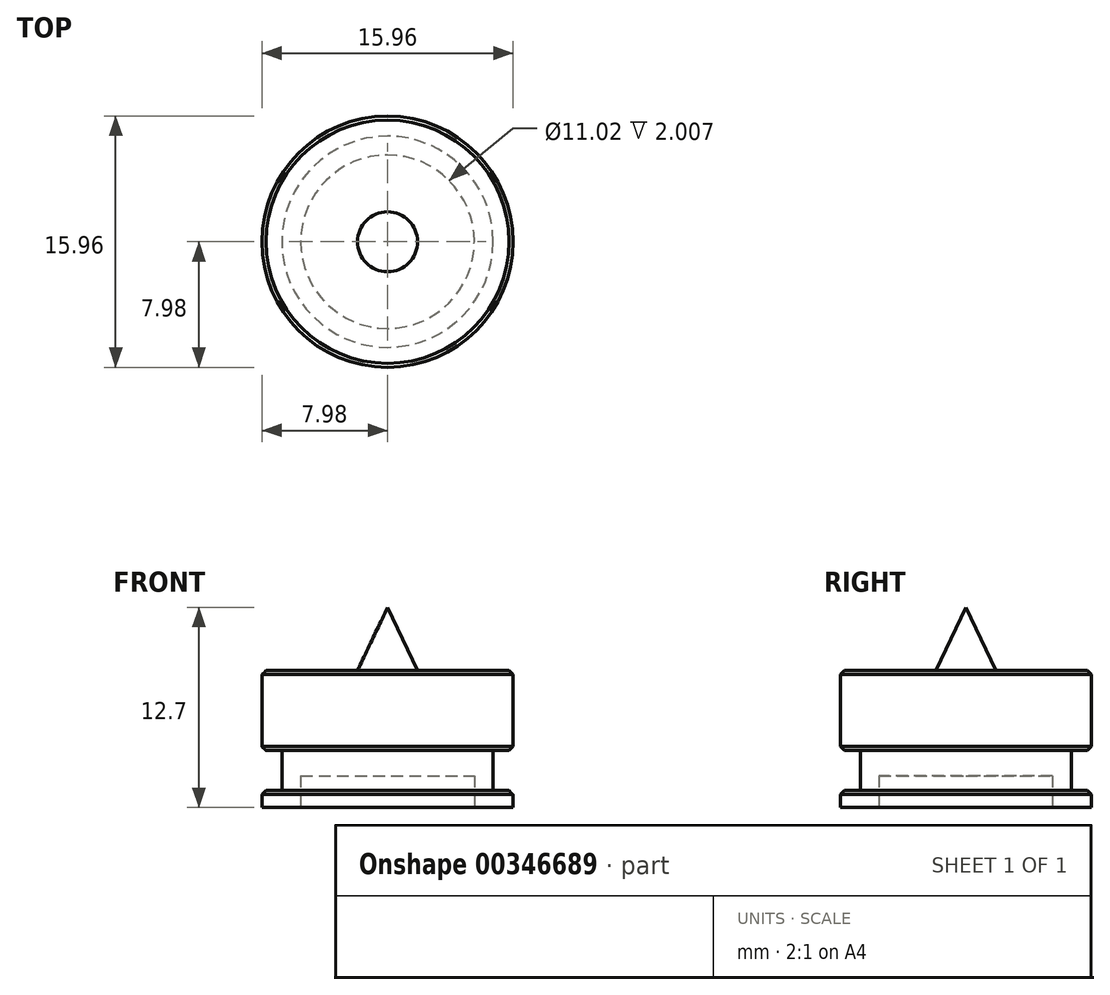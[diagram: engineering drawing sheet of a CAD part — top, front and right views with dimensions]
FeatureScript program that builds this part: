
annotation { "Feature Type Name" : "Feature", "Feature Type Description" : "" }
export const myFeature = defineFeature(function(context is Context, id is Id, definition is map)
    precondition{}
    {
        {
            var Q0;
            Q0=qCreatedBy(makeId("Front.planeOp"),FACE);
            var sketch = newSketch(context, id + "F0", { "sketchPlane" : qUnion([Q0])});
            skLineSegment(sketch, "E0", {"start": v(0, 2) * mm, "end": v(0, 12.7) * mm});
            skLineSegment(sketch, "E1", {"start": v(7.98, 8.69) * mm, "end": v(7.98, 3.6) * mm});
            skLineSegment(sketch, "E2", {"start": v(7.98, 0) * mm, "end": v(5.51, 0) * mm});
            skLineSegment(sketch, "E3", {"start": v(0, 12.7) * mm, "end": v(0, 8.69) * mm});
            skLineSegment(sketch, "E4", {"start": v(1.9, 8.69) * mm, "end": v(0, 12.7) * mm});
            skLineSegment(sketch, "E5", {"start": v(1.9, 8.69) * mm, "end": v(7.98, 8.69) * mm});
            skLineSegment(sketch, "E6", {"start": v(7.98, 1.07) * mm, "end": v(6.7, 1.07) * mm});
            skLineSegment(sketch, "E7", {"start": v(6.7, 1.07) * mm, "end": v(6.7, 3.6) * mm});
            skLineSegment(sketch, "E8", {"start": v(6.7, 3.6) * mm, "end": v(7.98, 3.6) * mm});
            skLineSegment(sketch, "E9.trimOffspring", {"start": v(7.98, 1.07) * mm, "end": v(7.98, 0) * mm});
            skLineSegment(sketch, "E10", {"start": v(5.51, 0) * mm, "end": v(5.51, 2) * mm});
            skLineSegment(sketch, "E11", {"start": v(5.51, 2) * mm, "end": v(0, 2) * mm});
            skPoint(sketch, "E12.orphan", {"position": v(0, 0) * mm});
            skSolve(sketch);
        }
        {
            var Q0;
            Q0 = qSketchRegion(id + "F0", true);
            var Q1;
            Q1=sQuery(id+"F0.wireOp",EDGE,"E0");
            revolve(context, id + "F1", {"entities" : qUnion([Q0]), "axis" : qUnion([Q1]), "revolveType" : RevolveType.FULL});
        }
        {
            var Q0;
            Q0=makeQuery(id+"F1.opRevolve","SWEPT_EDGE",EDGE,{"disambiguationData":[OSD([sQuery(id+"F0.wireOp",EDGE,"E5"),sQuery(id+"F0.wireOp",EDGE,"E1")])]});
            var Q1;
            Q1=makeQuery(id+"F1.opRevolve","SWEPT_EDGE",EDGE,{"disambiguationData":[OSD([sQuery(id+"F0.wireOp",EDGE,"E1"),sQuery(id+"F0.wireOp",EDGE,"E8")])]});
            var Q2;
            Q2=makeQuery(id+"F1.opRevolve","SWEPT_EDGE",EDGE,{"disambiguationData":[OSD([sQuery(id+"F0.wireOp",EDGE,"E6"),sQuery(id+"F0.wireOp",EDGE,"E9.trimOffspring")])]});
            chamfer(context, id + "F2", {"entities" : qUnion([Q0, Q1, Q2]), "width" : 0.25 * mm, "tangentPropagation" : true});
        }
    });
